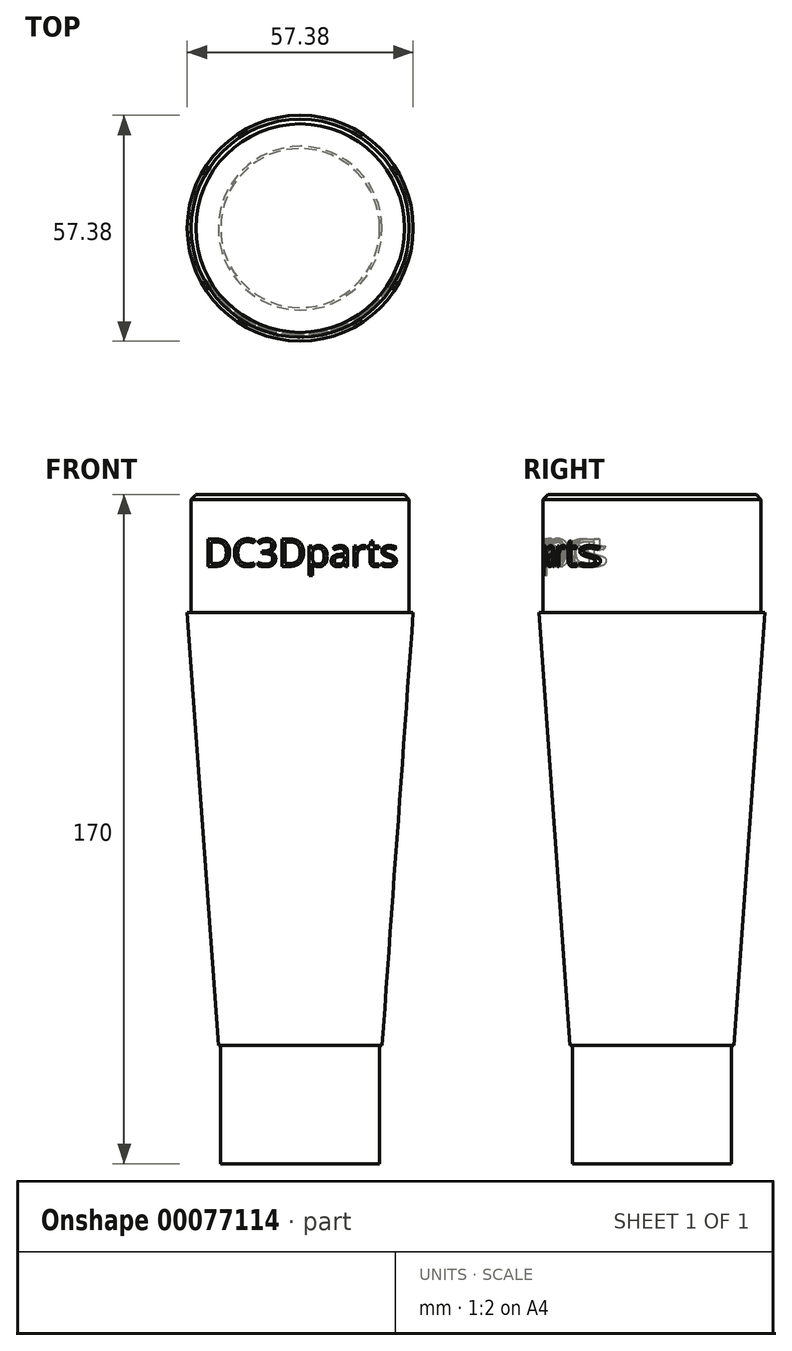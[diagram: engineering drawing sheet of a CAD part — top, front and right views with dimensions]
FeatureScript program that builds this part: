
annotation { "Feature Type Name" : "Feature", "Feature Type Description" : "" }
export const myFeature = defineFeature(function(context is Context, id is Id, definition is map)
    precondition{}
    {
        {
            var Q0;
            Q0=qCreatedBy(makeId("Front.planeOp"),FACE);
            var sketch = newSketch(context, id + "F0", { "sketchPlane" : qUnion([Q0])});
            skLineSegment(sketch, "E0", {"start": v(-27.68, 73.27) * mm, "end": v(-27.68, 43.27) * mm});
            skLineSegment(sketch, "E1", {"start": v(-27.68, 43.27) * mm, "end": v(-28.68, 43.27) * mm});
            skLineSegment(sketch, "E2", {"start": v(-28.68, 43.27) * mm, "end": v(-20.8, -66.73) * mm});
            skLineSegment(sketch, "E3", {"start": v(-20.8, -66.73) * mm, "end": v(-20.2, -66.73) * mm});
            skLineSegment(sketch, "E4", {"start": v(-20.2, -66.73) * mm, "end": v(-20.2, -96.73) * mm});
            skLineSegment(sketch, "E5", {"start": v(-20.2, -96.73) * mm, "end": v(0, -96.73) * mm});
            skLineSegment(sketch, "E6", {"start": v(-27.68, 73.27) * mm, "end": v(0, 73.27) * mm});
            skLineSegment(sketch, "E7", {"start": v(0, 94.78) * mm, "end": v(0, -99.97) * mm, "construction": true});
            skLineSegment(sketch, "E8", {"start": v(0, 73.27) * mm, "end": v(0, -96.73) * mm});
            skSolve(sketch);
        }
        {
            var Q0;
            Q0=makeQuery(id+"F0.imprint","IMPRINT",FACE,{"disambiguationData":[TD([[makeQuery(id+"F0.imprint","IMPRINT",EDGE,{"derivedFrom":sQuery(id+"F0.wireOp",EDGE,"E0")}),1.0]])]});
            var Q1;
            Q1=sQuery(id+"F0.wireOp",EDGE,"E7");
            revolve(context, id + "F1", {"entities" : qUnion([Q0]), "axis" : qUnion([Q1]), "revolveType" : RevolveType.FULL});
        }
        {
            var Q0;
            Q0=makeQuery(id+"F1.opRevolve","SWEPT_EDGE",EDGE,{"disambiguationData":[OSD([sQuery(id+"F0.wireOp",EDGE,"E0"),sQuery(id+"F0.wireOp",EDGE,"E6")])]});
            chamfer(context, id + "F2", {"entities" : qUnion([Q0]), "width" : 1.2 * mm, "tangentPropagation" : true});
        }
        {
            var Q0;
            Q0=qCreatedBy(makeId("Front.planeOp"),FACE);
            cPlane(context, id + "F3", {"entities" : qUnion([Q0]), "cplaneType" : CPlaneType.OFFSET, "offset" : 35 * mm, "width" : 150 * mm, "height" : 150 * mm});
        }
        {
            var Q0;
            Q0=qCreatedBy(id+"F3.planeOp",FACE);
            var sketch = newSketch(context, id + "F4", { "sketchPlane" : qUnion([Q0])});
            skText(sketch, "E9", { "text": "DC3Dparts", "fontName": "OpenSans-Regular.ttf"});
            const initialGuessF4  = {"E9": [-0.02441, 0.05502, 1, 0, 0.007]};
            skSetInitialGuess(sketch, initialGuessF4);
            skSolve(sketch);
        }
        {
            var Q0;
            Q0 = qSketchRegion(id + "F4", true);
            var Q1;
            Q1=qCreatedBy(makeId("Front.planeOp"),FACE);
            extrude(context, id + "F5", {"entities" : qUnion([Q0]), "endBound" : BoundingType.UP_TO_SURFACE, "oppositeDirection" : true, "depth" : 25 * mm, "endBoundEntityFace" : qUnion([Q1]), "offsetDistance" : 25 * mm});
        }
        {
            var Q0;
            Q0=qCreatedBy(makeId("Front.planeOp"),FACE);
            var sketch = newSketch(context, id + "F6", { "sketchPlane" : qUnion([Q0])});
            skLineSegment(sketch, "E10.bottom", {"start": v(0, 48.71) * mm, "end": v(-27, 48.71) * mm});
            skLineSegment(sketch, "E10.top", {"start": v(0, 76.33) * mm, "end": v(-27, 76.33) * mm});
            skLineSegment(sketch, "E10.left", {"start": v(0, 48.71) * mm, "end": v(0, 76.33) * mm});
            skLineSegment(sketch, "E10.right", {"start": v(-27, 48.71) * mm, "end": v(-27, 76.33) * mm});
            skSolve(sketch);
        }
        {
            var Q0;
            Q0=makeQuery(id+"F6.imprint","IMPRINT",FACE,{"disambiguationData":[TD([[makeQuery(id+"F6.imprint","IMPRINT",EDGE,{"derivedFrom":sQuery(id+"F6.wireOp",EDGE,"E10.bottom")}),-1.0]])]});
            var Q1;
            Q1=sQuery(id+"F6.wireOp",EDGE,"E10.left");
            revolve(context, id + "F7", {"entities" : qUnion([Q0]), "axis" : qUnion([Q1]), "revolveType" : RevolveType.FULL});
        }
        {
            var Q0;
            Q0=makeQuery(id+"F7.opRevolve","SWEPT_BODY",BODY,{"disambiguationData":[OSD([sQuery(id+"F6.wireOp",EDGE,"E10.bottom"),sQuery(id+"F6.wireOp",EDGE,"E10.top"),sQuery(id+"F6.wireOp",EDGE,"E10.left"),sQuery(id+"F6.wireOp",EDGE,"E10.right")])]});
            var Q1;
            Q1=makeQuery(id+"F5.opExtrude","SWEPT_BODY",BODY,{"disambiguationData":[OSD([sQuery(id+"F4.wireOp",EDGE,"E9.sketch_text.stroke-0"),sQuery(id+"F4.wireOp",EDGE,"E9.sketch_text.stroke-1"),sQuery(id+"F4.wireOp",EDGE,"E9.sketch_text.stroke-2"),sQuery(id+"F4.wireOp",EDGE,"E9.sketch_text.stroke-3"),sQuery(id+"F4.wireOp",EDGE,"E9.sketch_text.stroke-4"),sQuery(id+"F4.wireOp",EDGE,"E9.sketch_text.stroke-5"),sQuery(id+"F4.wireOp",EDGE,"E9.sketch_text.stroke-6"),sQuery(id+"F4.wireOp",EDGE,"E9.sketch_text.stroke-7"),sQuery(id+"F4.wireOp",EDGE,"E9.sketch_text.stroke-8"),sQuery(id+"F4.wireOp",EDGE,"E9.sketch_text.stroke-9"),sQuery(id+"F4.wireOp",EDGE,"E9.sketch_text.stroke-10"),sQuery(id+"F4.wireOp",EDGE,"E9.sketch_text.stroke-11"),sQuery(id+"F4.wireOp",EDGE,"E9.sketch_text.stroke-12"),sQuery(id+"F4.wireOp",EDGE,"E9.sketch_text.stroke-13")])]});
            var Q2;
            Q2=makeQuery(id+"F5.opExtrude","SWEPT_BODY",BODY,{"disambiguationData":[OSD([sQuery(id+"F4.wireOp",EDGE,"E9.sketch_text.stroke-14"),sQuery(id+"F4.wireOp",EDGE,"E9.sketch_text.stroke-15"),sQuery(id+"F4.wireOp",EDGE,"E9.sketch_text.stroke-16"),sQuery(id+"F4.wireOp",EDGE,"E9.sketch_text.stroke-17"),sQuery(id+"F4.wireOp",EDGE,"E9.sketch_text.stroke-18"),sQuery(id+"F4.wireOp",EDGE,"E9.sketch_text.stroke-19"),sQuery(id+"F4.wireOp",EDGE,"E9.sketch_text.stroke-20"),sQuery(id+"F4.wireOp",EDGE,"E9.sketch_text.stroke-21"),sQuery(id+"F4.wireOp",EDGE,"E9.sketch_text.stroke-22"),sQuery(id+"F4.wireOp",EDGE,"E9.sketch_text.stroke-23"),sQuery(id+"F4.wireOp",EDGE,"E9.sketch_text.stroke-24"),sQuery(id+"F4.wireOp",EDGE,"E9.sketch_text.stroke-25"),sQuery(id+"F4.wireOp",EDGE,"E9.sketch_text.stroke-26"),sQuery(id+"F4.wireOp",EDGE,"E9.sketch_text.stroke-27"),sQuery(id+"F4.wireOp",EDGE,"E9.sketch_text.stroke-28")])]});
            var Q3;
            Q3=makeQuery(id+"F5.opExtrude","SWEPT_BODY",BODY,{"disambiguationData":[OSD([sQuery(id+"F4.wireOp",EDGE,"E9.sketch_text.stroke-29"),sQuery(id+"F4.wireOp",EDGE,"E9.sketch_text.stroke-30"),sQuery(id+"F4.wireOp",EDGE,"E9.sketch_text.stroke-31"),sQuery(id+"F4.wireOp",EDGE,"E9.sketch_text.stroke-32"),sQuery(id+"F4.wireOp",EDGE,"E9.sketch_text.stroke-33"),sQuery(id+"F4.wireOp",EDGE,"E9.sketch_text.stroke-34"),sQuery(id+"F4.wireOp",EDGE,"E9.sketch_text.stroke-35"),sQuery(id+"F4.wireOp",EDGE,"E9.sketch_text.stroke-36"),sQuery(id+"F4.wireOp",EDGE,"E9.sketch_text.stroke-37"),sQuery(id+"F4.wireOp",EDGE,"E9.sketch_text.stroke-38"),sQuery(id+"F4.wireOp",EDGE,"E9.sketch_text.stroke-39"),sQuery(id+"F4.wireOp",EDGE,"E9.sketch_text.stroke-40"),sQuery(id+"F4.wireOp",EDGE,"E9.sketch_text.stroke-41"),sQuery(id+"F4.wireOp",EDGE,"E9.sketch_text.stroke-42"),sQuery(id+"F4.wireOp",EDGE,"E9.sketch_text.stroke-43"),sQuery(id+"F4.wireOp",EDGE,"E9.sketch_text.stroke-44"),sQuery(id+"F4.wireOp",EDGE,"E9.sketch_text.stroke-45"),sQuery(id+"F4.wireOp",EDGE,"E9.sketch_text.stroke-46"),sQuery(id+"F4.wireOp",EDGE,"E9.sketch_text.stroke-47"),sQuery(id+"F4.wireOp",EDGE,"E9.sketch_text.stroke-48"),sQuery(id+"F4.wireOp",EDGE,"E9.sketch_text.stroke-49"),sQuery(id+"F4.wireOp",EDGE,"E9.sketch_text.stroke-50"),sQuery(id+"F4.wireOp",EDGE,"E9.sketch_text.stroke-51"),sQuery(id+"F4.wireOp",EDGE,"E9.sketch_text.stroke-52"),sQuery(id+"F4.wireOp",EDGE,"E9.sketch_text.stroke-53"),sQuery(id+"F4.wireOp",EDGE,"E9.sketch_text.stroke-54"),sQuery(id+"F4.wireOp",EDGE,"E9.sketch_text.stroke-55"),sQuery(id+"F4.wireOp",EDGE,"E9.sketch_text.stroke-56")])]});
            var Q4;
            Q4=makeQuery(id+"F5.opExtrude","SWEPT_BODY",BODY,{"disambiguationData":[OSD([sQuery(id+"F4.wireOp",EDGE,"E9.sketch_text.stroke-57"),sQuery(id+"F4.wireOp",EDGE,"E9.sketch_text.stroke-58"),sQuery(id+"F4.wireOp",EDGE,"E9.sketch_text.stroke-59"),sQuery(id+"F4.wireOp",EDGE,"E9.sketch_text.stroke-60"),sQuery(id+"F4.wireOp",EDGE,"E9.sketch_text.stroke-61"),sQuery(id+"F4.wireOp",EDGE,"E9.sketch_text.stroke-62"),sQuery(id+"F4.wireOp",EDGE,"E9.sketch_text.stroke-63"),sQuery(id+"F4.wireOp",EDGE,"E9.sketch_text.stroke-64"),sQuery(id+"F4.wireOp",EDGE,"E9.sketch_text.stroke-65"),sQuery(id+"F4.wireOp",EDGE,"E9.sketch_text.stroke-66"),sQuery(id+"F4.wireOp",EDGE,"E9.sketch_text.stroke-67"),sQuery(id+"F4.wireOp",EDGE,"E9.sketch_text.stroke-68"),sQuery(id+"F4.wireOp",EDGE,"E9.sketch_text.stroke-69"),sQuery(id+"F4.wireOp",EDGE,"E9.sketch_text.stroke-70")])]});
            var Q5;
            Q5=makeQuery(id+"F5.opExtrude","SWEPT_BODY",BODY,{"disambiguationData":[OSD([sQuery(id+"F4.wireOp",EDGE,"E9.sketch_text.stroke-71"),sQuery(id+"F4.wireOp",EDGE,"E9.sketch_text.stroke-72"),sQuery(id+"F4.wireOp",EDGE,"E9.sketch_text.stroke-73"),sQuery(id+"F4.wireOp",EDGE,"E9.sketch_text.stroke-74"),sQuery(id+"F4.wireOp",EDGE,"E9.sketch_text.stroke-75"),sQuery(id+"F4.wireOp",EDGE,"E9.sketch_text.stroke-76"),sQuery(id+"F4.wireOp",EDGE,"E9.sketch_text.stroke-77"),sQuery(id+"F4.wireOp",EDGE,"E9.sketch_text.stroke-78"),sQuery(id+"F4.wireOp",EDGE,"E9.sketch_text.stroke-79"),sQuery(id+"F4.wireOp",EDGE,"E9.sketch_text.stroke-80"),sQuery(id+"F4.wireOp",EDGE,"E9.sketch_text.stroke-81"),sQuery(id+"F4.wireOp",EDGE,"E9.sketch_text.stroke-82"),sQuery(id+"F4.wireOp",EDGE,"E9.sketch_text.stroke-83"),sQuery(id+"F4.wireOp",EDGE,"E9.sketch_text.stroke-84"),sQuery(id+"F4.wireOp",EDGE,"E9.sketch_text.stroke-85"),sQuery(id+"F4.wireOp",EDGE,"E9.sketch_text.stroke-86"),sQuery(id+"F4.wireOp",EDGE,"E9.sketch_text.stroke-87"),sQuery(id+"F4.wireOp",EDGE,"E9.sketch_text.stroke-88"),sQuery(id+"F4.wireOp",EDGE,"E9.sketch_text.stroke-89"),sQuery(id+"F4.wireOp",EDGE,"E9.sketch_text.stroke-90"),sQuery(id+"F4.wireOp",EDGE,"E9.sketch_text.stroke-91"),sQuery(id+"F4.wireOp",EDGE,"E9.sketch_text.stroke-92"),sQuery(id+"F4.wireOp",EDGE,"E9.sketch_text.stroke-93"),sQuery(id+"F4.wireOp",EDGE,"E9.sketch_text.stroke-94"),sQuery(id+"F4.wireOp",EDGE,"E9.sketch_text.stroke-95")])]});
            var Q6;
            Q6=makeQuery(id+"F5.opExtrude","SWEPT_BODY",BODY,{"disambiguationData":[OSD([sQuery(id+"F4.wireOp",EDGE,"E9.sketch_text.stroke-96"),sQuery(id+"F4.wireOp",EDGE,"E9.sketch_text.stroke-97"),sQuery(id+"F4.wireOp",EDGE,"E9.sketch_text.stroke-98"),sQuery(id+"F4.wireOp",EDGE,"E9.sketch_text.stroke-99"),sQuery(id+"F4.wireOp",EDGE,"E9.sketch_text.stroke-100"),sQuery(id+"F4.wireOp",EDGE,"E9.sketch_text.stroke-101"),sQuery(id+"F4.wireOp",EDGE,"E9.sketch_text.stroke-102"),sQuery(id+"F4.wireOp",EDGE,"E9.sketch_text.stroke-103"),sQuery(id+"F4.wireOp",EDGE,"E9.sketch_text.stroke-104"),sQuery(id+"F4.wireOp",EDGE,"E9.sketch_text.stroke-105"),sQuery(id+"F4.wireOp",EDGE,"E9.sketch_text.stroke-106"),sQuery(id+"F4.wireOp",EDGE,"E9.sketch_text.stroke-107"),sQuery(id+"F4.wireOp",EDGE,"E9.sketch_text.stroke-108"),sQuery(id+"F4.wireOp",EDGE,"E9.sketch_text.stroke-109"),sQuery(id+"F4.wireOp",EDGE,"E9.sketch_text.stroke-110"),sQuery(id+"F4.wireOp",EDGE,"E9.sketch_text.stroke-111"),sQuery(id+"F4.wireOp",EDGE,"E9.sketch_text.stroke-112"),sQuery(id+"F4.wireOp",EDGE,"E9.sketch_text.stroke-113"),sQuery(id+"F4.wireOp",EDGE,"E9.sketch_text.stroke-114"),sQuery(id+"F4.wireOp",EDGE,"E9.sketch_text.stroke-115"),sQuery(id+"F4.wireOp",EDGE,"E9.sketch_text.stroke-116"),sQuery(id+"F4.wireOp",EDGE,"E9.sketch_text.stroke-117"),sQuery(id+"F4.wireOp",EDGE,"E9.sketch_text.stroke-118"),sQuery(id+"F4.wireOp",EDGE,"E9.sketch_text.stroke-119"),sQuery(id+"F4.wireOp",EDGE,"E9.sketch_text.stroke-120"),sQuery(id+"F4.wireOp",EDGE,"E9.sketch_text.stroke-121"),sQuery(id+"F4.wireOp",EDGE,"E9.sketch_text.stroke-122")])]});
            var Q7;
            Q7=makeQuery(id+"F5.opExtrude","SWEPT_BODY",BODY,{"disambiguationData":[OSD([sQuery(id+"F4.wireOp",EDGE,"E9.sketch_text.stroke-123"),sQuery(id+"F4.wireOp",EDGE,"E9.sketch_text.stroke-124"),sQuery(id+"F4.wireOp",EDGE,"E9.sketch_text.stroke-125"),sQuery(id+"F4.wireOp",EDGE,"E9.sketch_text.stroke-126"),sQuery(id+"F4.wireOp",EDGE,"E9.sketch_text.stroke-127"),sQuery(id+"F4.wireOp",EDGE,"E9.sketch_text.stroke-128"),sQuery(id+"F4.wireOp",EDGE,"E9.sketch_text.stroke-129"),sQuery(id+"F4.wireOp",EDGE,"E9.sketch_text.stroke-130"),sQuery(id+"F4.wireOp",EDGE,"E9.sketch_text.stroke-131"),sQuery(id+"F4.wireOp",EDGE,"E9.sketch_text.stroke-132"),sQuery(id+"F4.wireOp",EDGE,"E9.sketch_text.stroke-133"),sQuery(id+"F4.wireOp",EDGE,"E9.sketch_text.stroke-134"),sQuery(id+"F4.wireOp",EDGE,"E9.sketch_text.stroke-135")])]});
            var Q8;
            Q8=makeQuery(id+"F5.opExtrude","SWEPT_BODY",BODY,{"disambiguationData":[OSD([sQuery(id+"F4.wireOp",EDGE,"E9.sketch_text.stroke-136"),sQuery(id+"F4.wireOp",EDGE,"E9.sketch_text.stroke-137"),sQuery(id+"F4.wireOp",EDGE,"E9.sketch_text.stroke-138"),sQuery(id+"F4.wireOp",EDGE,"E9.sketch_text.stroke-139"),sQuery(id+"F4.wireOp",EDGE,"E9.sketch_text.stroke-140"),sQuery(id+"F4.wireOp",EDGE,"E9.sketch_text.stroke-141"),sQuery(id+"F4.wireOp",EDGE,"E9.sketch_text.stroke-142"),sQuery(id+"F4.wireOp",EDGE,"E9.sketch_text.stroke-143"),sQuery(id+"F4.wireOp",EDGE,"E9.sketch_text.stroke-144"),sQuery(id+"F4.wireOp",EDGE,"E9.sketch_text.stroke-145"),sQuery(id+"F4.wireOp",EDGE,"E9.sketch_text.stroke-146"),sQuery(id+"F4.wireOp",EDGE,"E9.sketch_text.stroke-147"),sQuery(id+"F4.wireOp",EDGE,"E9.sketch_text.stroke-148"),sQuery(id+"F4.wireOp",EDGE,"E9.sketch_text.stroke-149"),sQuery(id+"F4.wireOp",EDGE,"E9.sketch_text.stroke-150"),sQuery(id+"F4.wireOp",EDGE,"E9.sketch_text.stroke-151"),sQuery(id+"F4.wireOp",EDGE,"E9.sketch_text.stroke-152"),sQuery(id+"F4.wireOp",EDGE,"E9.sketch_text.stroke-153"),sQuery(id+"F4.wireOp",EDGE,"E9.sketch_text.stroke-154")])]});
            var Q9;
            Q9=makeQuery(id+"F5.opExtrude","SWEPT_BODY",BODY,{"disambiguationData":[OSD([sQuery(id+"F4.wireOp",EDGE,"E9.sketch_text.stroke-155"),sQuery(id+"F4.wireOp",EDGE,"E9.sketch_text.stroke-156"),sQuery(id+"F4.wireOp",EDGE,"E9.sketch_text.stroke-157"),sQuery(id+"F4.wireOp",EDGE,"E9.sketch_text.stroke-158"),sQuery(id+"F4.wireOp",EDGE,"E9.sketch_text.stroke-159"),sQuery(id+"F4.wireOp",EDGE,"E9.sketch_text.stroke-160"),sQuery(id+"F4.wireOp",EDGE,"E9.sketch_text.stroke-161"),sQuery(id+"F4.wireOp",EDGE,"E9.sketch_text.stroke-162"),sQuery(id+"F4.wireOp",EDGE,"E9.sketch_text.stroke-163"),sQuery(id+"F4.wireOp",EDGE,"E9.sketch_text.stroke-164"),sQuery(id+"F4.wireOp",EDGE,"E9.sketch_text.stroke-165"),sQuery(id+"F4.wireOp",EDGE,"E9.sketch_text.stroke-166"),sQuery(id+"F4.wireOp",EDGE,"E9.sketch_text.stroke-167"),sQuery(id+"F4.wireOp",EDGE,"E9.sketch_text.stroke-168"),sQuery(id+"F4.wireOp",EDGE,"E9.sketch_text.stroke-169"),sQuery(id+"F4.wireOp",EDGE,"E9.sketch_text.stroke-170"),sQuery(id+"F4.wireOp",EDGE,"E9.sketch_text.stroke-171"),sQuery(id+"F4.wireOp",EDGE,"E9.sketch_text.stroke-172"),sQuery(id+"F4.wireOp",EDGE,"E9.sketch_text.stroke-173"),sQuery(id+"F4.wireOp",EDGE,"E9.sketch_text.stroke-174"),sQuery(id+"F4.wireOp",EDGE,"E9.sketch_text.stroke-175"),sQuery(id+"F4.wireOp",EDGE,"E9.sketch_text.stroke-176"),sQuery(id+"F4.wireOp",EDGE,"E9.sketch_text.stroke-177"),sQuery(id+"F4.wireOp",EDGE,"E9.sketch_text.stroke-178"),sQuery(id+"F4.wireOp",EDGE,"E9.sketch_text.stroke-179")])]});
            booleanBodies(context, id + "F8", {"operationType" : BooleanOperationType.SUBTRACTION, "tools" : qUnion([Q0]), "targets" : qUnion([Q1, Q2, Q3, Q4, Q5, Q6, Q7, Q8, Q9])});
        }
        {
            var Q0;
            Q0=makeQuery(id+"F5.opExtrude","SWEPT_BODY",BODY,{"disambiguationData":[OSD([sQuery(id+"F4.wireOp",EDGE,"E9.sketch_text.stroke-0"),sQuery(id+"F4.wireOp",EDGE,"E9.sketch_text.stroke-1"),sQuery(id+"F4.wireOp",EDGE,"E9.sketch_text.stroke-2"),sQuery(id+"F4.wireOp",EDGE,"E9.sketch_text.stroke-3"),sQuery(id+"F4.wireOp",EDGE,"E9.sketch_text.stroke-4"),sQuery(id+"F4.wireOp",EDGE,"E9.sketch_text.stroke-5"),sQuery(id+"F4.wireOp",EDGE,"E9.sketch_text.stroke-6"),sQuery(id+"F4.wireOp",EDGE,"E9.sketch_text.stroke-7"),sQuery(id+"F4.wireOp",EDGE,"E9.sketch_text.stroke-8"),sQuery(id+"F4.wireOp",EDGE,"E9.sketch_text.stroke-9"),sQuery(id+"F4.wireOp",EDGE,"E9.sketch_text.stroke-10"),sQuery(id+"F4.wireOp",EDGE,"E9.sketch_text.stroke-11"),sQuery(id+"F4.wireOp",EDGE,"E9.sketch_text.stroke-12"),sQuery(id+"F4.wireOp",EDGE,"E9.sketch_text.stroke-13")])]});
            var Q1;
            Q1=makeQuery(id+"F5.opExtrude","SWEPT_BODY",BODY,{"disambiguationData":[OSD([sQuery(id+"F4.wireOp",EDGE,"E9.sketch_text.stroke-14"),sQuery(id+"F4.wireOp",EDGE,"E9.sketch_text.stroke-15"),sQuery(id+"F4.wireOp",EDGE,"E9.sketch_text.stroke-16"),sQuery(id+"F4.wireOp",EDGE,"E9.sketch_text.stroke-17"),sQuery(id+"F4.wireOp",EDGE,"E9.sketch_text.stroke-18"),sQuery(id+"F4.wireOp",EDGE,"E9.sketch_text.stroke-19"),sQuery(id+"F4.wireOp",EDGE,"E9.sketch_text.stroke-20"),sQuery(id+"F4.wireOp",EDGE,"E9.sketch_text.stroke-21"),sQuery(id+"F4.wireOp",EDGE,"E9.sketch_text.stroke-22"),sQuery(id+"F4.wireOp",EDGE,"E9.sketch_text.stroke-23"),sQuery(id+"F4.wireOp",EDGE,"E9.sketch_text.stroke-24"),sQuery(id+"F4.wireOp",EDGE,"E9.sketch_text.stroke-25"),sQuery(id+"F4.wireOp",EDGE,"E9.sketch_text.stroke-26"),sQuery(id+"F4.wireOp",EDGE,"E9.sketch_text.stroke-27"),sQuery(id+"F4.wireOp",EDGE,"E9.sketch_text.stroke-28")])]});
            var Q2;
            Q2=makeQuery(id+"F5.opExtrude","SWEPT_BODY",BODY,{"disambiguationData":[OSD([sQuery(id+"F4.wireOp",EDGE,"E9.sketch_text.stroke-29"),sQuery(id+"F4.wireOp",EDGE,"E9.sketch_text.stroke-30"),sQuery(id+"F4.wireOp",EDGE,"E9.sketch_text.stroke-31"),sQuery(id+"F4.wireOp",EDGE,"E9.sketch_text.stroke-32"),sQuery(id+"F4.wireOp",EDGE,"E9.sketch_text.stroke-33"),sQuery(id+"F4.wireOp",EDGE,"E9.sketch_text.stroke-34"),sQuery(id+"F4.wireOp",EDGE,"E9.sketch_text.stroke-35"),sQuery(id+"F4.wireOp",EDGE,"E9.sketch_text.stroke-36"),sQuery(id+"F4.wireOp",EDGE,"E9.sketch_text.stroke-37"),sQuery(id+"F4.wireOp",EDGE,"E9.sketch_text.stroke-38"),sQuery(id+"F4.wireOp",EDGE,"E9.sketch_text.stroke-39"),sQuery(id+"F4.wireOp",EDGE,"E9.sketch_text.stroke-40"),sQuery(id+"F4.wireOp",EDGE,"E9.sketch_text.stroke-41"),sQuery(id+"F4.wireOp",EDGE,"E9.sketch_text.stroke-42"),sQuery(id+"F4.wireOp",EDGE,"E9.sketch_text.stroke-43"),sQuery(id+"F4.wireOp",EDGE,"E9.sketch_text.stroke-44"),sQuery(id+"F4.wireOp",EDGE,"E9.sketch_text.stroke-45"),sQuery(id+"F4.wireOp",EDGE,"E9.sketch_text.stroke-46"),sQuery(id+"F4.wireOp",EDGE,"E9.sketch_text.stroke-47"),sQuery(id+"F4.wireOp",EDGE,"E9.sketch_text.stroke-48"),sQuery(id+"F4.wireOp",EDGE,"E9.sketch_text.stroke-49"),sQuery(id+"F4.wireOp",EDGE,"E9.sketch_text.stroke-50"),sQuery(id+"F4.wireOp",EDGE,"E9.sketch_text.stroke-51"),sQuery(id+"F4.wireOp",EDGE,"E9.sketch_text.stroke-52"),sQuery(id+"F4.wireOp",EDGE,"E9.sketch_text.stroke-53"),sQuery(id+"F4.wireOp",EDGE,"E9.sketch_text.stroke-54"),sQuery(id+"F4.wireOp",EDGE,"E9.sketch_text.stroke-55"),sQuery(id+"F4.wireOp",EDGE,"E9.sketch_text.stroke-56")])]});
            var Q3;
            Q3=makeQuery(id+"F5.opExtrude","SWEPT_BODY",BODY,{"disambiguationData":[OSD([sQuery(id+"F4.wireOp",EDGE,"E9.sketch_text.stroke-57"),sQuery(id+"F4.wireOp",EDGE,"E9.sketch_text.stroke-58"),sQuery(id+"F4.wireOp",EDGE,"E9.sketch_text.stroke-59"),sQuery(id+"F4.wireOp",EDGE,"E9.sketch_text.stroke-60"),sQuery(id+"F4.wireOp",EDGE,"E9.sketch_text.stroke-61"),sQuery(id+"F4.wireOp",EDGE,"E9.sketch_text.stroke-62"),sQuery(id+"F4.wireOp",EDGE,"E9.sketch_text.stroke-63"),sQuery(id+"F4.wireOp",EDGE,"E9.sketch_text.stroke-64"),sQuery(id+"F4.wireOp",EDGE,"E9.sketch_text.stroke-65"),sQuery(id+"F4.wireOp",EDGE,"E9.sketch_text.stroke-66"),sQuery(id+"F4.wireOp",EDGE,"E9.sketch_text.stroke-67"),sQuery(id+"F4.wireOp",EDGE,"E9.sketch_text.stroke-68"),sQuery(id+"F4.wireOp",EDGE,"E9.sketch_text.stroke-69"),sQuery(id+"F4.wireOp",EDGE,"E9.sketch_text.stroke-70")])]});
            var Q4;
            Q4=makeQuery(id+"F5.opExtrude","SWEPT_BODY",BODY,{"disambiguationData":[OSD([sQuery(id+"F4.wireOp",EDGE,"E9.sketch_text.stroke-71"),sQuery(id+"F4.wireOp",EDGE,"E9.sketch_text.stroke-72"),sQuery(id+"F4.wireOp",EDGE,"E9.sketch_text.stroke-73"),sQuery(id+"F4.wireOp",EDGE,"E9.sketch_text.stroke-74"),sQuery(id+"F4.wireOp",EDGE,"E9.sketch_text.stroke-75"),sQuery(id+"F4.wireOp",EDGE,"E9.sketch_text.stroke-76"),sQuery(id+"F4.wireOp",EDGE,"E9.sketch_text.stroke-77"),sQuery(id+"F4.wireOp",EDGE,"E9.sketch_text.stroke-78"),sQuery(id+"F4.wireOp",EDGE,"E9.sketch_text.stroke-79"),sQuery(id+"F4.wireOp",EDGE,"E9.sketch_text.stroke-80"),sQuery(id+"F4.wireOp",EDGE,"E9.sketch_text.stroke-81"),sQuery(id+"F4.wireOp",EDGE,"E9.sketch_text.stroke-82"),sQuery(id+"F4.wireOp",EDGE,"E9.sketch_text.stroke-83"),sQuery(id+"F4.wireOp",EDGE,"E9.sketch_text.stroke-84"),sQuery(id+"F4.wireOp",EDGE,"E9.sketch_text.stroke-85"),sQuery(id+"F4.wireOp",EDGE,"E9.sketch_text.stroke-86"),sQuery(id+"F4.wireOp",EDGE,"E9.sketch_text.stroke-87"),sQuery(id+"F4.wireOp",EDGE,"E9.sketch_text.stroke-88"),sQuery(id+"F4.wireOp",EDGE,"E9.sketch_text.stroke-89"),sQuery(id+"F4.wireOp",EDGE,"E9.sketch_text.stroke-90"),sQuery(id+"F4.wireOp",EDGE,"E9.sketch_text.stroke-91"),sQuery(id+"F4.wireOp",EDGE,"E9.sketch_text.stroke-92"),sQuery(id+"F4.wireOp",EDGE,"E9.sketch_text.stroke-93"),sQuery(id+"F4.wireOp",EDGE,"E9.sketch_text.stroke-94"),sQuery(id+"F4.wireOp",EDGE,"E9.sketch_text.stroke-95")])]});
            var Q5;
            Q5=makeQuery(id+"F5.opExtrude","SWEPT_BODY",BODY,{"disambiguationData":[OSD([sQuery(id+"F4.wireOp",EDGE,"E9.sketch_text.stroke-96"),sQuery(id+"F4.wireOp",EDGE,"E9.sketch_text.stroke-97"),sQuery(id+"F4.wireOp",EDGE,"E9.sketch_text.stroke-98"),sQuery(id+"F4.wireOp",EDGE,"E9.sketch_text.stroke-99"),sQuery(id+"F4.wireOp",EDGE,"E9.sketch_text.stroke-100"),sQuery(id+"F4.wireOp",EDGE,"E9.sketch_text.stroke-101"),sQuery(id+"F4.wireOp",EDGE,"E9.sketch_text.stroke-102"),sQuery(id+"F4.wireOp",EDGE,"E9.sketch_text.stroke-103"),sQuery(id+"F4.wireOp",EDGE,"E9.sketch_text.stroke-104"),sQuery(id+"F4.wireOp",EDGE,"E9.sketch_text.stroke-105"),sQuery(id+"F4.wireOp",EDGE,"E9.sketch_text.stroke-106"),sQuery(id+"F4.wireOp",EDGE,"E9.sketch_text.stroke-107"),sQuery(id+"F4.wireOp",EDGE,"E9.sketch_text.stroke-108"),sQuery(id+"F4.wireOp",EDGE,"E9.sketch_text.stroke-109"),sQuery(id+"F4.wireOp",EDGE,"E9.sketch_text.stroke-110"),sQuery(id+"F4.wireOp",EDGE,"E9.sketch_text.stroke-111"),sQuery(id+"F4.wireOp",EDGE,"E9.sketch_text.stroke-112"),sQuery(id+"F4.wireOp",EDGE,"E9.sketch_text.stroke-113"),sQuery(id+"F4.wireOp",EDGE,"E9.sketch_text.stroke-114"),sQuery(id+"F4.wireOp",EDGE,"E9.sketch_text.stroke-115"),sQuery(id+"F4.wireOp",EDGE,"E9.sketch_text.stroke-116"),sQuery(id+"F4.wireOp",EDGE,"E9.sketch_text.stroke-117"),sQuery(id+"F4.wireOp",EDGE,"E9.sketch_text.stroke-118"),sQuery(id+"F4.wireOp",EDGE,"E9.sketch_text.stroke-119"),sQuery(id+"F4.wireOp",EDGE,"E9.sketch_text.stroke-120"),sQuery(id+"F4.wireOp",EDGE,"E9.sketch_text.stroke-121"),sQuery(id+"F4.wireOp",EDGE,"E9.sketch_text.stroke-122")])]});
            var Q6;
            Q6=makeQuery(id+"F5.opExtrude","SWEPT_BODY",BODY,{"disambiguationData":[OSD([sQuery(id+"F4.wireOp",EDGE,"E9.sketch_text.stroke-123"),sQuery(id+"F4.wireOp",EDGE,"E9.sketch_text.stroke-124"),sQuery(id+"F4.wireOp",EDGE,"E9.sketch_text.stroke-125"),sQuery(id+"F4.wireOp",EDGE,"E9.sketch_text.stroke-126"),sQuery(id+"F4.wireOp",EDGE,"E9.sketch_text.stroke-127"),sQuery(id+"F4.wireOp",EDGE,"E9.sketch_text.stroke-128"),sQuery(id+"F4.wireOp",EDGE,"E9.sketch_text.stroke-129"),sQuery(id+"F4.wireOp",EDGE,"E9.sketch_text.stroke-130"),sQuery(id+"F4.wireOp",EDGE,"E9.sketch_text.stroke-131"),sQuery(id+"F4.wireOp",EDGE,"E9.sketch_text.stroke-132"),sQuery(id+"F4.wireOp",EDGE,"E9.sketch_text.stroke-133"),sQuery(id+"F4.wireOp",EDGE,"E9.sketch_text.stroke-134"),sQuery(id+"F4.wireOp",EDGE,"E9.sketch_text.stroke-135")])]});
            var Q7;
            Q7=makeQuery(id+"F5.opExtrude","SWEPT_BODY",BODY,{"disambiguationData":[OSD([sQuery(id+"F4.wireOp",EDGE,"E9.sketch_text.stroke-136"),sQuery(id+"F4.wireOp",EDGE,"E9.sketch_text.stroke-137"),sQuery(id+"F4.wireOp",EDGE,"E9.sketch_text.stroke-138"),sQuery(id+"F4.wireOp",EDGE,"E9.sketch_text.stroke-139"),sQuery(id+"F4.wireOp",EDGE,"E9.sketch_text.stroke-140"),sQuery(id+"F4.wireOp",EDGE,"E9.sketch_text.stroke-141"),sQuery(id+"F4.wireOp",EDGE,"E9.sketch_text.stroke-142"),sQuery(id+"F4.wireOp",EDGE,"E9.sketch_text.stroke-143"),sQuery(id+"F4.wireOp",EDGE,"E9.sketch_text.stroke-144"),sQuery(id+"F4.wireOp",EDGE,"E9.sketch_text.stroke-145"),sQuery(id+"F4.wireOp",EDGE,"E9.sketch_text.stroke-146"),sQuery(id+"F4.wireOp",EDGE,"E9.sketch_text.stroke-147"),sQuery(id+"F4.wireOp",EDGE,"E9.sketch_text.stroke-148"),sQuery(id+"F4.wireOp",EDGE,"E9.sketch_text.stroke-149"),sQuery(id+"F4.wireOp",EDGE,"E9.sketch_text.stroke-150"),sQuery(id+"F4.wireOp",EDGE,"E9.sketch_text.stroke-151"),sQuery(id+"F4.wireOp",EDGE,"E9.sketch_text.stroke-152"),sQuery(id+"F4.wireOp",EDGE,"E9.sketch_text.stroke-153"),sQuery(id+"F4.wireOp",EDGE,"E9.sketch_text.stroke-154")])]});
            var Q8;
            Q8=makeQuery(id+"F5.opExtrude","SWEPT_BODY",BODY,{"disambiguationData":[OSD([sQuery(id+"F4.wireOp",EDGE,"E9.sketch_text.stroke-155"),sQuery(id+"F4.wireOp",EDGE,"E9.sketch_text.stroke-156"),sQuery(id+"F4.wireOp",EDGE,"E9.sketch_text.stroke-157"),sQuery(id+"F4.wireOp",EDGE,"E9.sketch_text.stroke-158"),sQuery(id+"F4.wireOp",EDGE,"E9.sketch_text.stroke-159"),sQuery(id+"F4.wireOp",EDGE,"E9.sketch_text.stroke-160"),sQuery(id+"F4.wireOp",EDGE,"E9.sketch_text.stroke-161"),sQuery(id+"F4.wireOp",EDGE,"E9.sketch_text.stroke-162"),sQuery(id+"F4.wireOp",EDGE,"E9.sketch_text.stroke-163"),sQuery(id+"F4.wireOp",EDGE,"E9.sketch_text.stroke-164"),sQuery(id+"F4.wireOp",EDGE,"E9.sketch_text.stroke-165"),sQuery(id+"F4.wireOp",EDGE,"E9.sketch_text.stroke-166"),sQuery(id+"F4.wireOp",EDGE,"E9.sketch_text.stroke-167"),sQuery(id+"F4.wireOp",EDGE,"E9.sketch_text.stroke-168"),sQuery(id+"F4.wireOp",EDGE,"E9.sketch_text.stroke-169"),sQuery(id+"F4.wireOp",EDGE,"E9.sketch_text.stroke-170"),sQuery(id+"F4.wireOp",EDGE,"E9.sketch_text.stroke-171"),sQuery(id+"F4.wireOp",EDGE,"E9.sketch_text.stroke-172"),sQuery(id+"F4.wireOp",EDGE,"E9.sketch_text.stroke-173"),sQuery(id+"F4.wireOp",EDGE,"E9.sketch_text.stroke-174"),sQuery(id+"F4.wireOp",EDGE,"E9.sketch_text.stroke-175"),sQuery(id+"F4.wireOp",EDGE,"E9.sketch_text.stroke-176"),sQuery(id+"F4.wireOp",EDGE,"E9.sketch_text.stroke-177"),sQuery(id+"F4.wireOp",EDGE,"E9.sketch_text.stroke-178"),sQuery(id+"F4.wireOp",EDGE,"E9.sketch_text.stroke-179")])]});
            var Q9;
            Q9=makeQuery(id+"F1.opRevolve","SWEPT_BODY",BODY,{"disambiguationData":[OSD([sQuery(id+"F0.wireOp",EDGE,"E0"),sQuery(id+"F0.wireOp",EDGE,"E1"),sQuery(id+"F0.wireOp",EDGE,"E2"),sQuery(id+"F0.wireOp",EDGE,"E3"),sQuery(id+"F0.wireOp",EDGE,"E4"),sQuery(id+"F0.wireOp",EDGE,"E5"),sQuery(id+"F0.wireOp",EDGE,"E6"),sQuery(id+"F0.wireOp",EDGE,"E8")])]});
            booleanBodies(context, id + "F9", {"operationType" : BooleanOperationType.SUBTRACTION, "tools" : qUnion([Q0, Q1, Q2, Q3, Q4, Q5, Q6, Q7, Q8]), "targets" : qUnion([Q9])});
        }
    });
